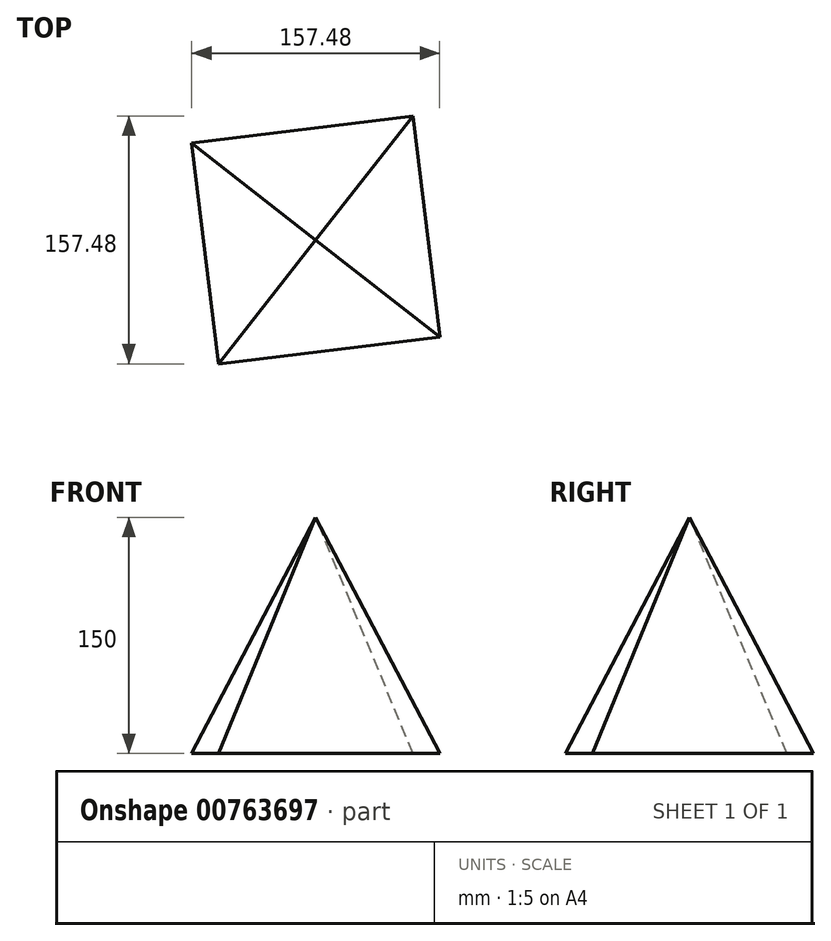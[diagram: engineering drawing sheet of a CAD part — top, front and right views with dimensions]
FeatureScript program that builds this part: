
annotation { "Feature Type Name" : "Feature", "Feature Type Description" : "" }
export const myFeature = defineFeature(function(context is Context, id is Id, definition is map)
    precondition{}
    {
        {
            var Q0;
            Q0=qCreatedBy(makeId("Top.planeOp"),FACE);
            var sketch = newSketch(context, id + "F0", { "sketchPlane" : qUnion([Q0])});
            skCircle(sketch, "E0.cCircle", {"center": v(0, 0) * mm, "radius": 100 * mm, "construction": true});
            skLineSegment(sketch, "E0.0", {"start": v(-78.74, 61.64) * mm, "end": v(61.64, 78.74) * mm});
            skLineSegment(sketch, "E0.1", {"start": v(61.64, 78.74) * mm, "end": v(78.74, -61.64) * mm});
            skLineSegment(sketch, "E0.2", {"start": v(78.74, -61.64) * mm, "end": v(-61.64, -78.74) * mm});
            skLineSegment(sketch, "E0.3", {"start": v(-61.64, -78.74) * mm, "end": v(-78.74, 61.64) * mm});
            skSolve(sketch);
        }
        {
            var Q0;
            Q0=qCreatedBy(makeId("Top.planeOp"),FACE);
            cPlane(context, id + "F1", {"entities" : qUnion([Q0]), "cplaneType" : CPlaneType.OFFSET, "offset" : 150 * mm, "width" : 150 * mm, "height" : 150 * mm});
        }
        {
            var Q0;
            Q0=qCreatedBy(id+"F1.planeOp",FACE);
            var sketch = newSketch(context, id + "F2", { "sketchPlane" : qUnion([Q0])});
            skPoint(sketch, "E1.0", {"position": v(0, 0) * mm});
            skSolve(sketch);
        }
        {
            var Q0;
            Q0=makeQuery(id+"F0.imprint","IMPRINT",FACE,{"disambiguationData":[TD([[makeQuery(id+"F0.imprint","IMPRINT",EDGE,{"derivedFrom":sQuery(id+"F0.wireOp",EDGE,"E0.0")}),-1.0]])]});
            var Q1;
            Q1=sQuery(id+"F2.wireOp",VERTEX,"E1.0");
            loft(context, id + "F3", {"sheetProfilesArray" : [{ "sheetProfileEntities" : qUnion([Q0]) }, { "sheetProfileEntities" : qUnion([Q1]) }]});
        }
    });
